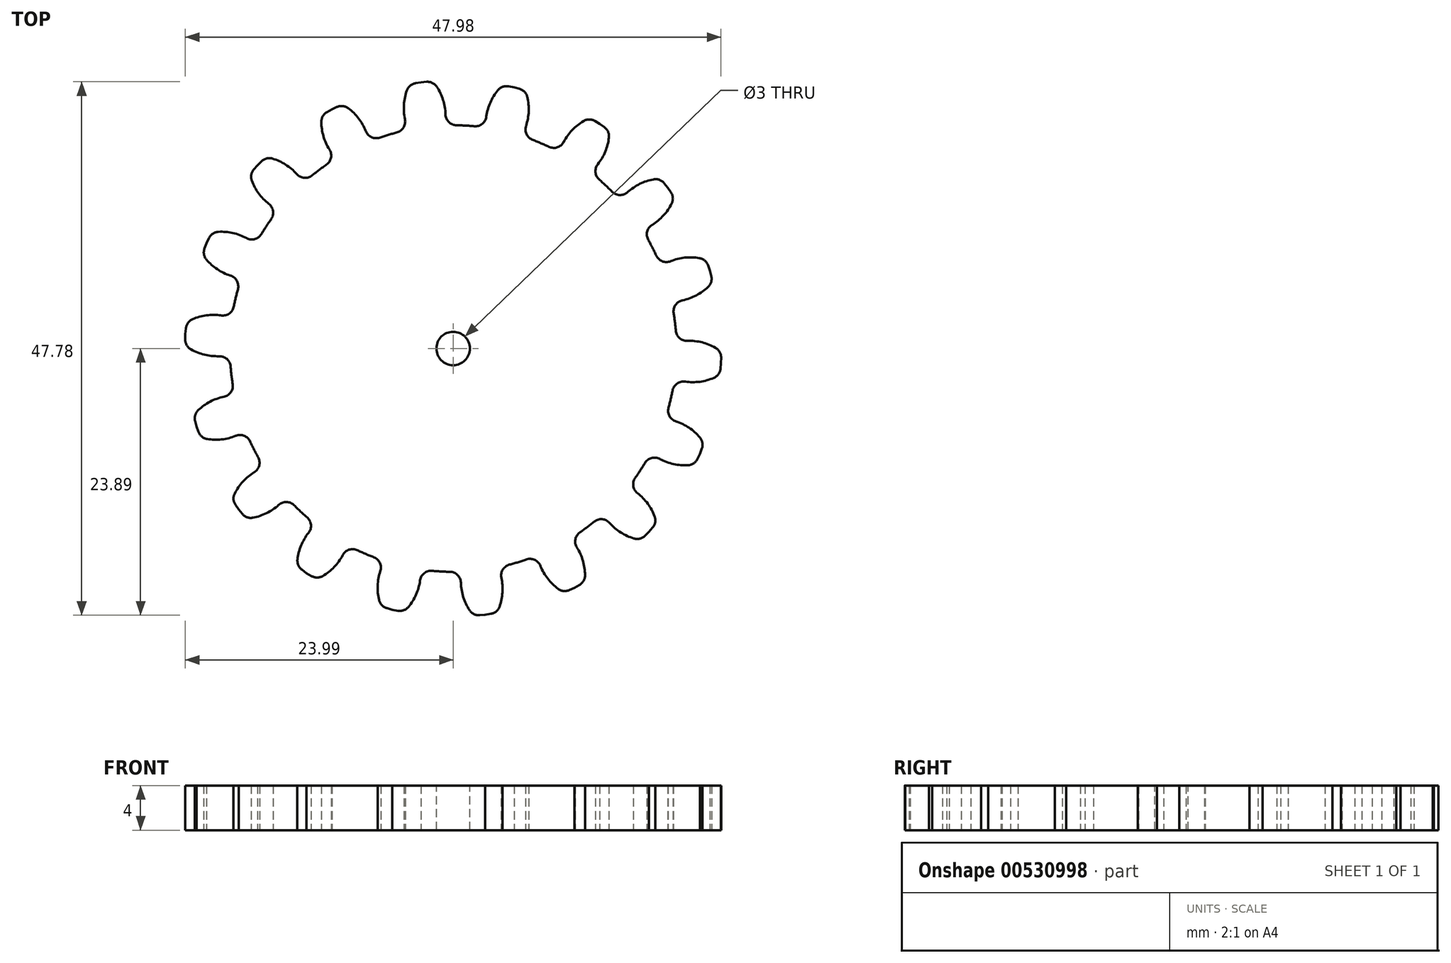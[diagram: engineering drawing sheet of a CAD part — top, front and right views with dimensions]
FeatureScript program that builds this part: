
annotation { "Feature Type Name" : "Feature", "Feature Type Description" : "" }
export const myFeature = defineFeature(function(context is Context, id is Id, definition is map)
    precondition{}
    {
        {
            var Q0;
            Q0=qCreatedBy(makeId("Top.planeOp"),FACE);
            var sketch = newSketch(context, id + "F0", { "sketchPlane" : qUnion([Q0])});
            skCircle(sketch, "E0", {"center": v(0, 0) * mm, "radius": 20 * mm, "construction": true});
            skLineSegment(sketch, "E1", {"start": v(0, 0) * mm, "end": v(29.94, 3.61) * mm, "construction": true});
            skLineSegment(sketch, "E2", {"start": v(0, 0) * mm, "end": v(27.72, -1.51) * mm, "construction": true});
            skLineSegment(sketch, "E3", {"start": v(0, 0) * mm, "end": v(20.99, 0.69) * mm, "construction": true});
            skLineSegment(sketch, "E4", {"start": v(0, 0) * mm, "end": v(24, -0.26) * mm, "construction": true});
            skArc(sketch, "E5", {"start": v(23.48, 0.07) * mm, "mid": v(22.28, 0.55) * mm, "end": v(20.99, 0.69) * mm});
            skArc(sketch, "E6", {"start": v(19.86, 2.4) * mm, "mid": v(19.9, 2) * mm, "end": v(19.94, 1.6) * mm});
            skLineSegment(sketch, "E7", {"start": v(20.96, 0.69) * mm, "end": v(20.99, 0.69) * mm});
            skLineSegment(sketch, "E8", {"start": v(24, -0.8) * mm, "end": v(23.99, -1.3) * mm});
            skLineSegment(sketch, "E9", {"start": v(0, 0) * mm, "end": v(19.86, 2.4) * mm});
            skLineSegment(sketch, "E10.MirrorCS", {"start": v(0, 0) * mm, "end": v(19.48, -4.54) * mm});
            skArc(sketch, "E11.MirrorCS", {"start": v(19.48, -4.54) * mm, "mid": v(19.56, -4.15) * mm, "end": v(19.64, -3.77) * mm});
            skLineSegment(sketch, "E12.MirrorCS", {"start": v(20.77, -2.96) * mm, "end": v(20.79, -2.97) * mm});
            skArc(sketch, "E13.MirrorCS", {"start": v(23.34, -2.63) * mm, "mid": v(22.09, -2.97) * mm, "end": v(20.79, -2.97) * mm});
            skLineSegment(sketch, "E14.MirrorCS", {"start": v(23.94, -1.8) * mm, "end": v(23.99, -1.3) * mm});
            skPoint(sketch, "E15.visualSharp", {"position": v(19.8, -2.83) * mm});
            skArc(sketch, "E15.filletArc", {"start": v(20.77, -2.96) * mm, "mid": v(20.04, -3.14) * mm, "end": v(19.64, -3.77) * mm});
            skPoint(sketch, "E16.visualSharp", {"position": v(19.99, 0.65) * mm});
            skArc(sketch, "E16.filletArc", {"start": v(19.94, 1.6) * mm, "mid": v(20.27, 0.94) * mm, "end": v(20.96, 0.69) * mm});
            skPoint(sketch, "E17.visualSharp", {"position": v(24, -0.26) * mm});
            skArc(sketch, "E17.filletArc", {"start": v(24, -0.8) * mm, "mid": v(23.86, -0.3) * mm, "end": v(23.48, 0.07) * mm});
            skPoint(sketch, "E18.visualSharp", {"position": v(23.88, -2.35) * mm});
            skArc(sketch, "E18.filletArc", {"start": v(23.34, -2.63) * mm, "mid": v(23.75, -2.3) * mm, "end": v(23.94, -1.8) * mm});
            skSolve(sketch);
        }
        {
            var Q0;
            Q0 = qSketchRegion(id + "F0", true);
            extrude(context, id + "F1", {"entities" : qUnion([Q0]), "depth" : 4 * mm, "offsetDistance" : 25 * mm});
        }
        {
            var Q0;
            Q0=makeQuery(id+"F1.opExtrude","SWEPT_BODY",BODY,{"disambiguationData":[OSD([sQuery(id+"F0.wireOp",EDGE,"E5"),sQuery(id+"F0.wireOp",EDGE,"E6"),sQuery(id+"F0.wireOp",EDGE,"E7"),sQuery(id+"F0.wireOp",EDGE,"E8"),sQuery(id+"F0.wireOp",EDGE,"E9"),sQuery(id+"F0.wireOp",EDGE,"E10.MirrorCS"),sQuery(id+"F0.wireOp",EDGE,"E11.MirrorCS"),sQuery(id+"F0.wireOp",EDGE,"E12.MirrorCS"),sQuery(id+"F0.wireOp",EDGE,"E13.MirrorCS"),sQuery(id+"F0.wireOp",EDGE,"E14.MirrorCS"),sQuery(id+"F0.wireOp",EDGE,"E15.filletArc"),sQuery(id+"F0.wireOp",EDGE,"E16.filletArc"),sQuery(id+"F0.wireOp",EDGE,"E17.filletArc"),sQuery(id+"F0.wireOp",EDGE,"E18.filletArc")])]});
            var Q1;
            Q1=makeQuery(id+"F1.opExtrude","SWEPT_EDGE",EDGE,{"disambiguationData":[OSD([sQuery(id+"F0.wireOp",EDGE,"E9"),sQuery(id+"F0.wireOp",EDGE,"E10.MirrorCS")])]});
            circularPattern(context, id + "F2", {"entities" : qUnion([Q0]), "axis" : qUnion([Q1]), "angle" : 360 * degree, "instanceCount" : 18, "oppositeDirection" : true, "equalSpace" : true, "computeTransformsWithoutBuiltin" : true});
        }
        {
            var Q0;
            Q0=makeQuery(id+"F2.opPattern","COPY",BODY,{"derivedFrom":makeQuery(id+"F1.opExtrude","SWEPT_BODY",BODY,{"disambiguationData":[OSD([sQuery(id+"F0.wireOp",EDGE,"E5"),sQuery(id+"F0.wireOp",EDGE,"E6"),sQuery(id+"F0.wireOp",EDGE,"E7"),sQuery(id+"F0.wireOp",EDGE,"E8"),sQuery(id+"F0.wireOp",EDGE,"E9"),sQuery(id+"F0.wireOp",EDGE,"E10.MirrorCS"),sQuery(id+"F0.wireOp",EDGE,"E11.MirrorCS"),sQuery(id+"F0.wireOp",EDGE,"E12.MirrorCS"),sQuery(id+"F0.wireOp",EDGE,"E13.MirrorCS"),sQuery(id+"F0.wireOp",EDGE,"E14.MirrorCS"),sQuery(id+"F0.wireOp",EDGE,"E15.filletArc"),sQuery(id+"F0.wireOp",EDGE,"E16.filletArc"),sQuery(id+"F0.wireOp",EDGE,"E17.filletArc"),sQuery(id+"F0.wireOp",EDGE,"E18.filletArc")])]}),"instanceName":"6"});
            var Q1;
            Q1=makeQuery(id+"F2.opPattern","COPY",BODY,{"derivedFrom":makeQuery(id+"F1.opExtrude","SWEPT_BODY",BODY,{"disambiguationData":[OSD([sQuery(id+"F0.wireOp",EDGE,"E5"),sQuery(id+"F0.wireOp",EDGE,"E6"),sQuery(id+"F0.wireOp",EDGE,"E7"),sQuery(id+"F0.wireOp",EDGE,"E8"),sQuery(id+"F0.wireOp",EDGE,"E9"),sQuery(id+"F0.wireOp",EDGE,"E10.MirrorCS"),sQuery(id+"F0.wireOp",EDGE,"E11.MirrorCS"),sQuery(id+"F0.wireOp",EDGE,"E12.MirrorCS"),sQuery(id+"F0.wireOp",EDGE,"E13.MirrorCS"),sQuery(id+"F0.wireOp",EDGE,"E14.MirrorCS"),sQuery(id+"F0.wireOp",EDGE,"E15.filletArc"),sQuery(id+"F0.wireOp",EDGE,"E16.filletArc"),sQuery(id+"F0.wireOp",EDGE,"E17.filletArc"),sQuery(id+"F0.wireOp",EDGE,"E18.filletArc")])]}),"instanceName":"12"});
            var Q2;
            Q2=makeQuery(id+"F2.opPattern","COPY",BODY,{"derivedFrom":makeQuery(id+"F1.opExtrude","SWEPT_BODY",BODY,{"disambiguationData":[OSD([sQuery(id+"F0.wireOp",EDGE,"E5"),sQuery(id+"F0.wireOp",EDGE,"E6"),sQuery(id+"F0.wireOp",EDGE,"E7"),sQuery(id+"F0.wireOp",EDGE,"E8"),sQuery(id+"F0.wireOp",EDGE,"E9"),sQuery(id+"F0.wireOp",EDGE,"E10.MirrorCS"),sQuery(id+"F0.wireOp",EDGE,"E11.MirrorCS"),sQuery(id+"F0.wireOp",EDGE,"E12.MirrorCS"),sQuery(id+"F0.wireOp",EDGE,"E13.MirrorCS"),sQuery(id+"F0.wireOp",EDGE,"E14.MirrorCS"),sQuery(id+"F0.wireOp",EDGE,"E15.filletArc"),sQuery(id+"F0.wireOp",EDGE,"E16.filletArc"),sQuery(id+"F0.wireOp",EDGE,"E17.filletArc"),sQuery(id+"F0.wireOp",EDGE,"E18.filletArc")])]}),"instanceName":"14"});
            var Q3;
            Q3=makeQuery(id+"F2.opPattern","COPY",BODY,{"derivedFrom":makeQuery(id+"F1.opExtrude","SWEPT_BODY",BODY,{"disambiguationData":[OSD([sQuery(id+"F0.wireOp",EDGE,"E5"),sQuery(id+"F0.wireOp",EDGE,"E6"),sQuery(id+"F0.wireOp",EDGE,"E7"),sQuery(id+"F0.wireOp",EDGE,"E8"),sQuery(id+"F0.wireOp",EDGE,"E9"),sQuery(id+"F0.wireOp",EDGE,"E10.MirrorCS"),sQuery(id+"F0.wireOp",EDGE,"E11.MirrorCS"),sQuery(id+"F0.wireOp",EDGE,"E12.MirrorCS"),sQuery(id+"F0.wireOp",EDGE,"E13.MirrorCS"),sQuery(id+"F0.wireOp",EDGE,"E14.MirrorCS"),sQuery(id+"F0.wireOp",EDGE,"E15.filletArc"),sQuery(id+"F0.wireOp",EDGE,"E16.filletArc"),sQuery(id+"F0.wireOp",EDGE,"E17.filletArc"),sQuery(id+"F0.wireOp",EDGE,"E18.filletArc")])]}),"instanceName":"13"});
            var Q4;
            Q4=makeQuery(id+"F2.opPattern","COPY",BODY,{"derivedFrom":makeQuery(id+"F1.opExtrude","SWEPT_BODY",BODY,{"disambiguationData":[OSD([sQuery(id+"F0.wireOp",EDGE,"E5"),sQuery(id+"F0.wireOp",EDGE,"E6"),sQuery(id+"F0.wireOp",EDGE,"E7"),sQuery(id+"F0.wireOp",EDGE,"E8"),sQuery(id+"F0.wireOp",EDGE,"E9"),sQuery(id+"F0.wireOp",EDGE,"E10.MirrorCS"),sQuery(id+"F0.wireOp",EDGE,"E11.MirrorCS"),sQuery(id+"F0.wireOp",EDGE,"E12.MirrorCS"),sQuery(id+"F0.wireOp",EDGE,"E13.MirrorCS"),sQuery(id+"F0.wireOp",EDGE,"E14.MirrorCS"),sQuery(id+"F0.wireOp",EDGE,"E15.filletArc"),sQuery(id+"F0.wireOp",EDGE,"E16.filletArc"),sQuery(id+"F0.wireOp",EDGE,"E17.filletArc"),sQuery(id+"F0.wireOp",EDGE,"E18.filletArc")])]}),"instanceName":"9"});
            var Q5;
            Q5=makeQuery(id+"F2.opPattern","COPY",BODY,{"derivedFrom":makeQuery(id+"F1.opExtrude","SWEPT_BODY",BODY,{"disambiguationData":[OSD([sQuery(id+"F0.wireOp",EDGE,"E5"),sQuery(id+"F0.wireOp",EDGE,"E6"),sQuery(id+"F0.wireOp",EDGE,"E7"),sQuery(id+"F0.wireOp",EDGE,"E8"),sQuery(id+"F0.wireOp",EDGE,"E9"),sQuery(id+"F0.wireOp",EDGE,"E10.MirrorCS"),sQuery(id+"F0.wireOp",EDGE,"E11.MirrorCS"),sQuery(id+"F0.wireOp",EDGE,"E12.MirrorCS"),sQuery(id+"F0.wireOp",EDGE,"E13.MirrorCS"),sQuery(id+"F0.wireOp",EDGE,"E14.MirrorCS"),sQuery(id+"F0.wireOp",EDGE,"E15.filletArc"),sQuery(id+"F0.wireOp",EDGE,"E16.filletArc"),sQuery(id+"F0.wireOp",EDGE,"E17.filletArc"),sQuery(id+"F0.wireOp",EDGE,"E18.filletArc")])]}),"instanceName":"10"});
            var Q6;
            Q6=makeQuery(id+"F2.opPattern","COPY",BODY,{"derivedFrom":makeQuery(id+"F1.opExtrude","SWEPT_BODY",BODY,{"disambiguationData":[OSD([sQuery(id+"F0.wireOp",EDGE,"E5"),sQuery(id+"F0.wireOp",EDGE,"E6"),sQuery(id+"F0.wireOp",EDGE,"E7"),sQuery(id+"F0.wireOp",EDGE,"E8"),sQuery(id+"F0.wireOp",EDGE,"E9"),sQuery(id+"F0.wireOp",EDGE,"E10.MirrorCS"),sQuery(id+"F0.wireOp",EDGE,"E11.MirrorCS"),sQuery(id+"F0.wireOp",EDGE,"E12.MirrorCS"),sQuery(id+"F0.wireOp",EDGE,"E13.MirrorCS"),sQuery(id+"F0.wireOp",EDGE,"E14.MirrorCS"),sQuery(id+"F0.wireOp",EDGE,"E15.filletArc"),sQuery(id+"F0.wireOp",EDGE,"E16.filletArc"),sQuery(id+"F0.wireOp",EDGE,"E17.filletArc"),sQuery(id+"F0.wireOp",EDGE,"E18.filletArc")])]}),"instanceName":"11"});
            var Q7;
            Q7=makeQuery(id+"F2.opPattern","COPY",BODY,{"derivedFrom":makeQuery(id+"F1.opExtrude","SWEPT_BODY",BODY,{"disambiguationData":[OSD([sQuery(id+"F0.wireOp",EDGE,"E5"),sQuery(id+"F0.wireOp",EDGE,"E6"),sQuery(id+"F0.wireOp",EDGE,"E7"),sQuery(id+"F0.wireOp",EDGE,"E8"),sQuery(id+"F0.wireOp",EDGE,"E9"),sQuery(id+"F0.wireOp",EDGE,"E10.MirrorCS"),sQuery(id+"F0.wireOp",EDGE,"E11.MirrorCS"),sQuery(id+"F0.wireOp",EDGE,"E12.MirrorCS"),sQuery(id+"F0.wireOp",EDGE,"E13.MirrorCS"),sQuery(id+"F0.wireOp",EDGE,"E14.MirrorCS"),sQuery(id+"F0.wireOp",EDGE,"E15.filletArc"),sQuery(id+"F0.wireOp",EDGE,"E16.filletArc"),sQuery(id+"F0.wireOp",EDGE,"E17.filletArc"),sQuery(id+"F0.wireOp",EDGE,"E18.filletArc")])]}),"instanceName":"5"});
            var Q8;
            Q8=makeQuery(id+"F2.opPattern","COPY",BODY,{"derivedFrom":makeQuery(id+"F1.opExtrude","SWEPT_BODY",BODY,{"disambiguationData":[OSD([sQuery(id+"F0.wireOp",EDGE,"E5"),sQuery(id+"F0.wireOp",EDGE,"E6"),sQuery(id+"F0.wireOp",EDGE,"E7"),sQuery(id+"F0.wireOp",EDGE,"E8"),sQuery(id+"F0.wireOp",EDGE,"E9"),sQuery(id+"F0.wireOp",EDGE,"E10.MirrorCS"),sQuery(id+"F0.wireOp",EDGE,"E11.MirrorCS"),sQuery(id+"F0.wireOp",EDGE,"E12.MirrorCS"),sQuery(id+"F0.wireOp",EDGE,"E13.MirrorCS"),sQuery(id+"F0.wireOp",EDGE,"E14.MirrorCS"),sQuery(id+"F0.wireOp",EDGE,"E15.filletArc"),sQuery(id+"F0.wireOp",EDGE,"E16.filletArc"),sQuery(id+"F0.wireOp",EDGE,"E17.filletArc"),sQuery(id+"F0.wireOp",EDGE,"E18.filletArc")])]}),"instanceName":"16"});
            var Q9;
            Q9=makeQuery(id+"F2.opPattern","COPY",BODY,{"derivedFrom":makeQuery(id+"F1.opExtrude","SWEPT_BODY",BODY,{"disambiguationData":[OSD([sQuery(id+"F0.wireOp",EDGE,"E5"),sQuery(id+"F0.wireOp",EDGE,"E6"),sQuery(id+"F0.wireOp",EDGE,"E7"),sQuery(id+"F0.wireOp",EDGE,"E8"),sQuery(id+"F0.wireOp",EDGE,"E9"),sQuery(id+"F0.wireOp",EDGE,"E10.MirrorCS"),sQuery(id+"F0.wireOp",EDGE,"E11.MirrorCS"),sQuery(id+"F0.wireOp",EDGE,"E12.MirrorCS"),sQuery(id+"F0.wireOp",EDGE,"E13.MirrorCS"),sQuery(id+"F0.wireOp",EDGE,"E14.MirrorCS"),sQuery(id+"F0.wireOp",EDGE,"E15.filletArc"),sQuery(id+"F0.wireOp",EDGE,"E16.filletArc"),sQuery(id+"F0.wireOp",EDGE,"E17.filletArc"),sQuery(id+"F0.wireOp",EDGE,"E18.filletArc")])]}),"instanceName":"17"});
            var Q10;
            Q10=makeQuery(id+"F2.opPattern","COPY",BODY,{"derivedFrom":makeQuery(id+"F1.opExtrude","SWEPT_BODY",BODY,{"disambiguationData":[OSD([sQuery(id+"F0.wireOp",EDGE,"E5"),sQuery(id+"F0.wireOp",EDGE,"E6"),sQuery(id+"F0.wireOp",EDGE,"E7"),sQuery(id+"F0.wireOp",EDGE,"E8"),sQuery(id+"F0.wireOp",EDGE,"E9"),sQuery(id+"F0.wireOp",EDGE,"E10.MirrorCS"),sQuery(id+"F0.wireOp",EDGE,"E11.MirrorCS"),sQuery(id+"F0.wireOp",EDGE,"E12.MirrorCS"),sQuery(id+"F0.wireOp",EDGE,"E13.MirrorCS"),sQuery(id+"F0.wireOp",EDGE,"E14.MirrorCS"),sQuery(id+"F0.wireOp",EDGE,"E15.filletArc"),sQuery(id+"F0.wireOp",EDGE,"E16.filletArc"),sQuery(id+"F0.wireOp",EDGE,"E17.filletArc"),sQuery(id+"F0.wireOp",EDGE,"E18.filletArc")])]}),"instanceName":"15"});
            var Q11;
            Q11=makeQuery(id+"F2.opPattern","COPY",BODY,{"derivedFrom":makeQuery(id+"F1.opExtrude","SWEPT_BODY",BODY,{"disambiguationData":[OSD([sQuery(id+"F0.wireOp",EDGE,"E5"),sQuery(id+"F0.wireOp",EDGE,"E6"),sQuery(id+"F0.wireOp",EDGE,"E7"),sQuery(id+"F0.wireOp",EDGE,"E8"),sQuery(id+"F0.wireOp",EDGE,"E9"),sQuery(id+"F0.wireOp",EDGE,"E10.MirrorCS"),sQuery(id+"F0.wireOp",EDGE,"E11.MirrorCS"),sQuery(id+"F0.wireOp",EDGE,"E12.MirrorCS"),sQuery(id+"F0.wireOp",EDGE,"E13.MirrorCS"),sQuery(id+"F0.wireOp",EDGE,"E14.MirrorCS"),sQuery(id+"F0.wireOp",EDGE,"E15.filletArc"),sQuery(id+"F0.wireOp",EDGE,"E16.filletArc"),sQuery(id+"F0.wireOp",EDGE,"E17.filletArc"),sQuery(id+"F0.wireOp",EDGE,"E18.filletArc")])]}),"instanceName":"7"});
            var Q12;
            Q12=makeQuery(id+"F2.opPattern","COPY",BODY,{"derivedFrom":makeQuery(id+"F1.opExtrude","SWEPT_BODY",BODY,{"disambiguationData":[OSD([sQuery(id+"F0.wireOp",EDGE,"E5"),sQuery(id+"F0.wireOp",EDGE,"E6"),sQuery(id+"F0.wireOp",EDGE,"E7"),sQuery(id+"F0.wireOp",EDGE,"E8"),sQuery(id+"F0.wireOp",EDGE,"E9"),sQuery(id+"F0.wireOp",EDGE,"E10.MirrorCS"),sQuery(id+"F0.wireOp",EDGE,"E11.MirrorCS"),sQuery(id+"F0.wireOp",EDGE,"E12.MirrorCS"),sQuery(id+"F0.wireOp",EDGE,"E13.MirrorCS"),sQuery(id+"F0.wireOp",EDGE,"E14.MirrorCS"),sQuery(id+"F0.wireOp",EDGE,"E15.filletArc"),sQuery(id+"F0.wireOp",EDGE,"E16.filletArc"),sQuery(id+"F0.wireOp",EDGE,"E17.filletArc"),sQuery(id+"F0.wireOp",EDGE,"E18.filletArc")])]}),"instanceName":"8"});
            var Q13;
            Q13=makeQuery(id+"F2.opPattern","COPY",BODY,{"derivedFrom":makeQuery(id+"F1.opExtrude","SWEPT_BODY",BODY,{"disambiguationData":[OSD([sQuery(id+"F0.wireOp",EDGE,"E5"),sQuery(id+"F0.wireOp",EDGE,"E6"),sQuery(id+"F0.wireOp",EDGE,"E7"),sQuery(id+"F0.wireOp",EDGE,"E8"),sQuery(id+"F0.wireOp",EDGE,"E9"),sQuery(id+"F0.wireOp",EDGE,"E10.MirrorCS"),sQuery(id+"F0.wireOp",EDGE,"E11.MirrorCS"),sQuery(id+"F0.wireOp",EDGE,"E12.MirrorCS"),sQuery(id+"F0.wireOp",EDGE,"E13.MirrorCS"),sQuery(id+"F0.wireOp",EDGE,"E14.MirrorCS"),sQuery(id+"F0.wireOp",EDGE,"E15.filletArc"),sQuery(id+"F0.wireOp",EDGE,"E16.filletArc"),sQuery(id+"F0.wireOp",EDGE,"E17.filletArc"),sQuery(id+"F0.wireOp",EDGE,"E18.filletArc")])]}),"instanceName":"2"});
            var Q14;
            Q14=makeQuery(id+"F2.opPattern","COPY",BODY,{"derivedFrom":makeQuery(id+"F1.opExtrude","SWEPT_BODY",BODY,{"disambiguationData":[OSD([sQuery(id+"F0.wireOp",EDGE,"E5"),sQuery(id+"F0.wireOp",EDGE,"E6"),sQuery(id+"F0.wireOp",EDGE,"E7"),sQuery(id+"F0.wireOp",EDGE,"E8"),sQuery(id+"F0.wireOp",EDGE,"E9"),sQuery(id+"F0.wireOp",EDGE,"E10.MirrorCS"),sQuery(id+"F0.wireOp",EDGE,"E11.MirrorCS"),sQuery(id+"F0.wireOp",EDGE,"E12.MirrorCS"),sQuery(id+"F0.wireOp",EDGE,"E13.MirrorCS"),sQuery(id+"F0.wireOp",EDGE,"E14.MirrorCS"),sQuery(id+"F0.wireOp",EDGE,"E15.filletArc"),sQuery(id+"F0.wireOp",EDGE,"E16.filletArc"),sQuery(id+"F0.wireOp",EDGE,"E17.filletArc"),sQuery(id+"F0.wireOp",EDGE,"E18.filletArc")])]}),"instanceName":"3"});
            var Q15;
            Q15=makeQuery(id+"F2.opPattern","COPY",BODY,{"derivedFrom":makeQuery(id+"F1.opExtrude","SWEPT_BODY",BODY,{"disambiguationData":[OSD([sQuery(id+"F0.wireOp",EDGE,"E5"),sQuery(id+"F0.wireOp",EDGE,"E6"),sQuery(id+"F0.wireOp",EDGE,"E7"),sQuery(id+"F0.wireOp",EDGE,"E8"),sQuery(id+"F0.wireOp",EDGE,"E9"),sQuery(id+"F0.wireOp",EDGE,"E10.MirrorCS"),sQuery(id+"F0.wireOp",EDGE,"E11.MirrorCS"),sQuery(id+"F0.wireOp",EDGE,"E12.MirrorCS"),sQuery(id+"F0.wireOp",EDGE,"E13.MirrorCS"),sQuery(id+"F0.wireOp",EDGE,"E14.MirrorCS"),sQuery(id+"F0.wireOp",EDGE,"E15.filletArc"),sQuery(id+"F0.wireOp",EDGE,"E16.filletArc"),sQuery(id+"F0.wireOp",EDGE,"E17.filletArc"),sQuery(id+"F0.wireOp",EDGE,"E18.filletArc")])]}),"instanceName":"4"});
            var Q16;
            Q16=makeQuery(id+"F2.opPattern","COPY",BODY,{"derivedFrom":makeQuery(id+"F1.opExtrude","SWEPT_BODY",BODY,{"disambiguationData":[OSD([sQuery(id+"F0.wireOp",EDGE,"E5"),sQuery(id+"F0.wireOp",EDGE,"E6"),sQuery(id+"F0.wireOp",EDGE,"E7"),sQuery(id+"F0.wireOp",EDGE,"E8"),sQuery(id+"F0.wireOp",EDGE,"E9"),sQuery(id+"F0.wireOp",EDGE,"E10.MirrorCS"),sQuery(id+"F0.wireOp",EDGE,"E11.MirrorCS"),sQuery(id+"F0.wireOp",EDGE,"E12.MirrorCS"),sQuery(id+"F0.wireOp",EDGE,"E13.MirrorCS"),sQuery(id+"F0.wireOp",EDGE,"E14.MirrorCS"),sQuery(id+"F0.wireOp",EDGE,"E15.filletArc"),sQuery(id+"F0.wireOp",EDGE,"E16.filletArc"),sQuery(id+"F0.wireOp",EDGE,"E17.filletArc"),sQuery(id+"F0.wireOp",EDGE,"E18.filletArc")])]}),"instanceName":"1"});
            var Q17;
            Q17=makeQuery(id+"F1.opExtrude","SWEPT_BODY",BODY,{"disambiguationData":[OSD([sQuery(id+"F0.wireOp",EDGE,"E5"),sQuery(id+"F0.wireOp",EDGE,"E6"),sQuery(id+"F0.wireOp",EDGE,"E7"),sQuery(id+"F0.wireOp",EDGE,"E8"),sQuery(id+"F0.wireOp",EDGE,"E9"),sQuery(id+"F0.wireOp",EDGE,"E10.MirrorCS"),sQuery(id+"F0.wireOp",EDGE,"E11.MirrorCS"),sQuery(id+"F0.wireOp",EDGE,"E12.MirrorCS"),sQuery(id+"F0.wireOp",EDGE,"E13.MirrorCS"),sQuery(id+"F0.wireOp",EDGE,"E14.MirrorCS"),sQuery(id+"F0.wireOp",EDGE,"E15.filletArc"),sQuery(id+"F0.wireOp",EDGE,"E16.filletArc"),sQuery(id+"F0.wireOp",EDGE,"E17.filletArc"),sQuery(id+"F0.wireOp",EDGE,"E18.filletArc")])]});
            booleanBodies(context, id + "F3", {"operationType" : BooleanOperationType.UNION, "tools" : qUnion([Q0, Q1, Q2, Q3, Q4, Q5, Q6, Q7, Q8, Q9, Q10, Q11, Q12, Q13, Q14, Q15, Q16, Q17])});
        }
        {
            var Q0;
            {var subQ0=makeQuery(id+"F1.opExtrude","CAP_FACE",FACE,{"disambiguationData":[OSD([sQuery(id+"F0.wireOp",EDGE,"E5"),sQuery(id+"F0.wireOp",EDGE,"E6"),sQuery(id+"F0.wireOp",EDGE,"E7"),sQuery(id+"F0.wireOp",EDGE,"E8"),sQuery(id+"F0.wireOp",EDGE,"E9"),sQuery(id+"F0.wireOp",EDGE,"E10.MirrorCS"),sQuery(id+"F0.wireOp",EDGE,"E11.MirrorCS"),sQuery(id+"F0.wireOp",EDGE,"E12.MirrorCS"),sQuery(id+"F0.wireOp",EDGE,"E13.MirrorCS"),sQuery(id+"F0.wireOp",EDGE,"E14.MirrorCS"),sQuery(id+"F0.wireOp",EDGE,"E15.filletArc"),sQuery(id+"F0.wireOp",EDGE,"E16.filletArc"),sQuery(id+"F0.wireOp",EDGE,"E17.filletArc"),sQuery(id+"F0.wireOp",EDGE,"E18.filletArc")])],"isStart":false});Q0=makeQuery(id+"F3.opBoolean","MERGE",FACE,{"derivedFrom":[subQ0,makeQuery(id+"F2.opPattern","COPY",FACE,{"derivedFrom":subQ0,"instanceName":"1"}),makeQuery(id+"F2.opPattern","COPY",FACE,{"derivedFrom":subQ0,"instanceName":"2"}),makeQuery(id+"F2.opPattern","COPY",FACE,{"derivedFrom":subQ0,"instanceName":"3"}),makeQuery(id+"F2.opPattern","COPY",FACE,{"derivedFrom":subQ0,"instanceName":"4"}),makeQuery(id+"F2.opPattern","COPY",FACE,{"derivedFrom":subQ0,"instanceName":"5"}),makeQuery(id+"F2.opPattern","COPY",FACE,{"derivedFrom":subQ0,"instanceName":"6"}),makeQuery(id+"F2.opPattern","COPY",FACE,{"derivedFrom":subQ0,"instanceName":"7"}),makeQuery(id+"F2.opPattern","COPY",FACE,{"derivedFrom":subQ0,"instanceName":"8"}),makeQuery(id+"F2.opPattern","COPY",FACE,{"derivedFrom":subQ0,"instanceName":"9"}),makeQuery(id+"F2.opPattern","COPY",FACE,{"derivedFrom":subQ0,"instanceName":"10"}),makeQuery(id+"F2.opPattern","COPY",FACE,{"derivedFrom":subQ0,"instanceName":"11"}),makeQuery(id+"F2.opPattern","COPY",FACE,{"derivedFrom":subQ0,"instanceName":"12"}),makeQuery(id+"F2.opPattern","COPY",FACE,{"derivedFrom":subQ0,"instanceName":"13"}),makeQuery(id+"F2.opPattern","COPY",FACE,{"derivedFrom":subQ0,"instanceName":"14"}),makeQuery(id+"F2.opPattern","COPY",FACE,{"derivedFrom":subQ0,"instanceName":"15"}),makeQuery(id+"F2.opPattern","COPY",FACE,{"derivedFrom":subQ0,"instanceName":"16"}),makeQuery(id+"F2.opPattern","COPY",FACE,{"derivedFrom":subQ0,"instanceName":"17"})]});}
            var sketch = newSketch(context, id + "F4", { "sketchPlane" : qUnion([Q0])});
            skCircle(sketch, "E19", {"center": v(0, 0) * mm, "radius": 1.5 * mm});
            skSolve(sketch);
        }
        {
            var Q0;
            Q0 = qSketchRegion(id + "F4", true);
            var Q1;
            {var subQ0=makeQuery(id+"F1.opExtrude","CAP_FACE",FACE,{"disambiguationData":[OSD([sQuery(id+"F0.wireOp",EDGE,"E5"),sQuery(id+"F0.wireOp",EDGE,"E6"),sQuery(id+"F0.wireOp",EDGE,"E7"),sQuery(id+"F0.wireOp",EDGE,"E8"),sQuery(id+"F0.wireOp",EDGE,"E9"),sQuery(id+"F0.wireOp",EDGE,"E10.MirrorCS"),sQuery(id+"F0.wireOp",EDGE,"E11.MirrorCS"),sQuery(id+"F0.wireOp",EDGE,"E12.MirrorCS"),sQuery(id+"F0.wireOp",EDGE,"E13.MirrorCS"),sQuery(id+"F0.wireOp",EDGE,"E14.MirrorCS"),sQuery(id+"F0.wireOp",EDGE,"E15.filletArc"),sQuery(id+"F0.wireOp",EDGE,"E16.filletArc"),sQuery(id+"F0.wireOp",EDGE,"E17.filletArc"),sQuery(id+"F0.wireOp",EDGE,"E18.filletArc")])],"isStart":true});Q1=makeQuery(id+"F3.opBoolean","MERGE",FACE,{"derivedFrom":[subQ0,makeQuery(id+"F2.opPattern","COPY",FACE,{"derivedFrom":subQ0,"instanceName":"1"}),makeQuery(id+"F2.opPattern","COPY",FACE,{"derivedFrom":subQ0,"instanceName":"2"}),makeQuery(id+"F2.opPattern","COPY",FACE,{"derivedFrom":subQ0,"instanceName":"3"}),makeQuery(id+"F2.opPattern","COPY",FACE,{"derivedFrom":subQ0,"instanceName":"4"}),makeQuery(id+"F2.opPattern","COPY",FACE,{"derivedFrom":subQ0,"instanceName":"5"}),makeQuery(id+"F2.opPattern","COPY",FACE,{"derivedFrom":subQ0,"instanceName":"6"}),makeQuery(id+"F2.opPattern","COPY",FACE,{"derivedFrom":subQ0,"instanceName":"7"}),makeQuery(id+"F2.opPattern","COPY",FACE,{"derivedFrom":subQ0,"instanceName":"8"}),makeQuery(id+"F2.opPattern","COPY",FACE,{"derivedFrom":subQ0,"instanceName":"9"}),makeQuery(id+"F2.opPattern","COPY",FACE,{"derivedFrom":subQ0,"instanceName":"10"}),makeQuery(id+"F2.opPattern","COPY",FACE,{"derivedFrom":subQ0,"instanceName":"11"}),makeQuery(id+"F2.opPattern","COPY",FACE,{"derivedFrom":subQ0,"instanceName":"12"}),makeQuery(id+"F2.opPattern","COPY",FACE,{"derivedFrom":subQ0,"instanceName":"13"}),makeQuery(id+"F2.opPattern","COPY",FACE,{"derivedFrom":subQ0,"instanceName":"14"}),makeQuery(id+"F2.opPattern","COPY",FACE,{"derivedFrom":subQ0,"instanceName":"15"}),makeQuery(id+"F2.opPattern","COPY",FACE,{"derivedFrom":subQ0,"instanceName":"16"}),makeQuery(id+"F2.opPattern","COPY",FACE,{"derivedFrom":subQ0,"instanceName":"17"})]});}
            extrude(context, id + "F5", {"entities" : qUnion([Q0]), "operationType" : NewBodyOperationType.REMOVE, "endBound" : BoundingType.UP_TO_SURFACE, "oppositeDirection" : true, "depth" : 25 * mm, "endBoundEntityFace" : qUnion([Q1]), "offsetDistance" : 25 * mm});
        }
        {
            var Q0;
            Q0=makeQuery(id+"F2.opPattern","COPY",BODY,{"derivedFrom":makeQuery(id+"F1.opExtrude","SWEPT_BODY",BODY,{"disambiguationData":[OSD([sQuery(id+"F0.wireOp",EDGE,"E5"),sQuery(id+"F0.wireOp",EDGE,"E6"),sQuery(id+"F0.wireOp",EDGE,"E7"),sQuery(id+"F0.wireOp",EDGE,"E8"),sQuery(id+"F0.wireOp",EDGE,"E9"),sQuery(id+"F0.wireOp",EDGE,"E10.MirrorCS"),sQuery(id+"F0.wireOp",EDGE,"E11.MirrorCS"),sQuery(id+"F0.wireOp",EDGE,"E12.MirrorCS"),sQuery(id+"F0.wireOp",EDGE,"E13.MirrorCS"),sQuery(id+"F0.wireOp",EDGE,"E14.MirrorCS"),sQuery(id+"F0.wireOp",EDGE,"E15.filletArc"),sQuery(id+"F0.wireOp",EDGE,"E16.filletArc"),sQuery(id+"F0.wireOp",EDGE,"E17.filletArc"),sQuery(id+"F0.wireOp",EDGE,"E18.filletArc")])]}),"instanceName":"6"});
            transform(context, id + "F6", {"entities" : qUnion([Q0]), "transformType" : TransformType.TRANSLATION_3D, "dx" : 0 * mm, "dy" : 0 * mm, "dz" : 0 * mm, "makeCopy" : true});
        }
        {
            var Q0;
            Q0=makeQuery(id+"F6.opPattern","COPY",BODY,{"derivedFrom":makeQuery(id+"F2.opPattern","COPY",BODY,{"derivedFrom":makeQuery(id+"F1.opExtrude","SWEPT_BODY",BODY,{"disambiguationData":[OSD([sQuery(id+"F0.wireOp",EDGE,"E5"),sQuery(id+"F0.wireOp",EDGE,"E6"),sQuery(id+"F0.wireOp",EDGE,"E7"),sQuery(id+"F0.wireOp",EDGE,"E8"),sQuery(id+"F0.wireOp",EDGE,"E9"),sQuery(id+"F0.wireOp",EDGE,"E10.MirrorCS"),sQuery(id+"F0.wireOp",EDGE,"E11.MirrorCS"),sQuery(id+"F0.wireOp",EDGE,"E12.MirrorCS"),sQuery(id+"F0.wireOp",EDGE,"E13.MirrorCS"),sQuery(id+"F0.wireOp",EDGE,"E14.MirrorCS"),sQuery(id+"F0.wireOp",EDGE,"E15.filletArc"),sQuery(id+"F0.wireOp",EDGE,"E16.filletArc"),sQuery(id+"F0.wireOp",EDGE,"E17.filletArc"),sQuery(id+"F0.wireOp",EDGE,"E18.filletArc")])]}),"instanceName":"6"}),"instanceName":"1"});
            deleteBodies(context, id + "F7", {"entities" : qUnion([Q0])});
        }
    });
